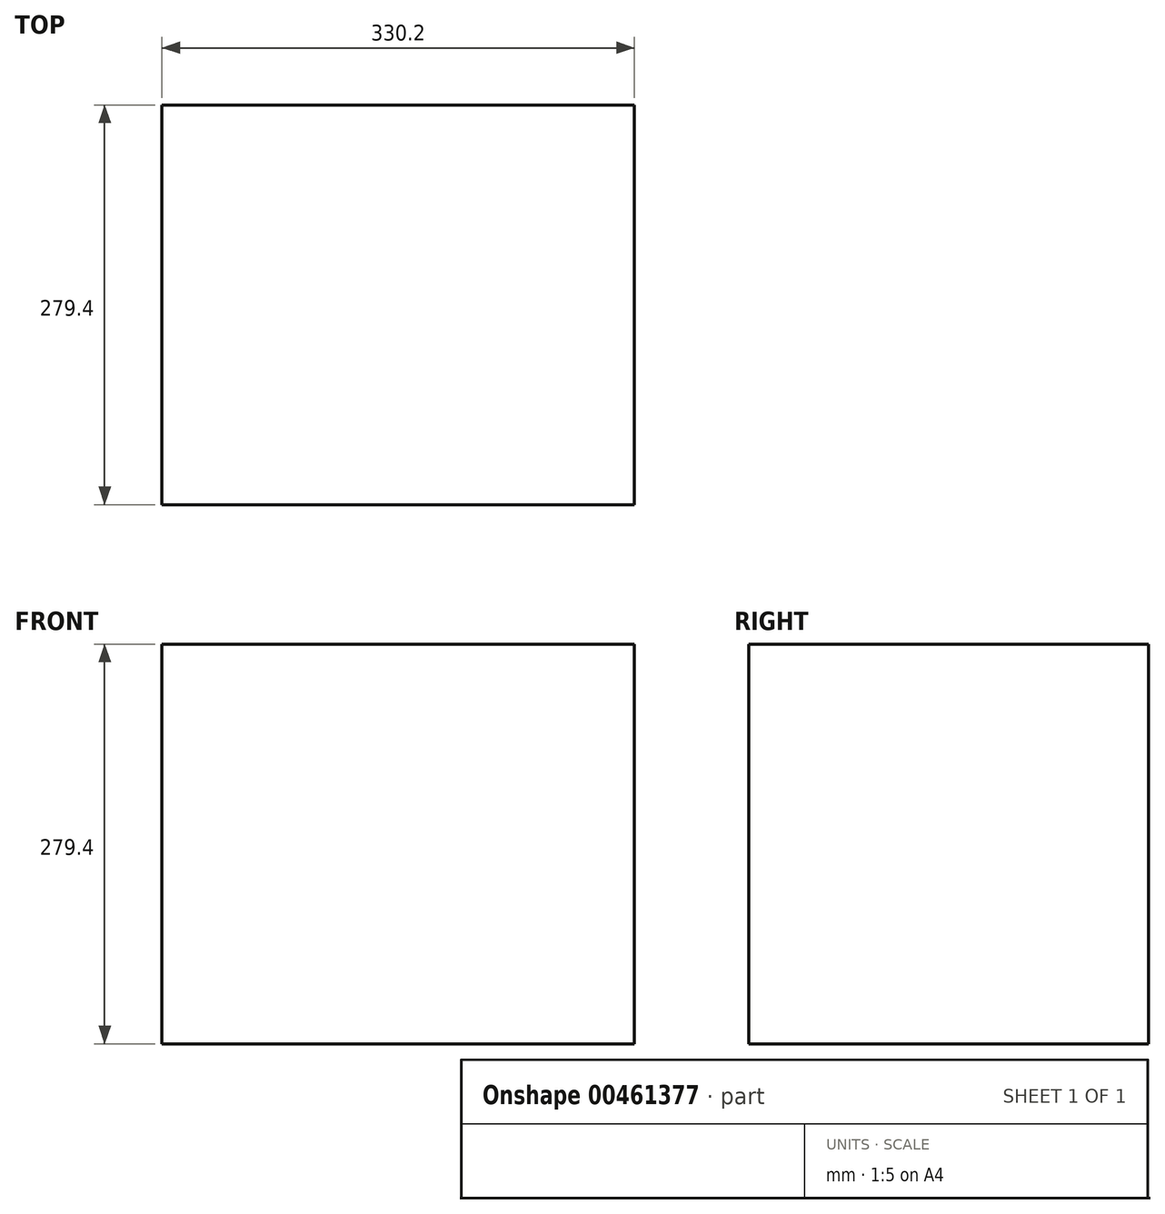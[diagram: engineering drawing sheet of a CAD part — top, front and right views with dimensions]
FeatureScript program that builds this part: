
annotation { "Feature Type Name" : "Feature", "Feature Type Description" : "" }
export const myFeature = defineFeature(function(context is Context, id is Id, definition is map)
    precondition{}
    {
        {
            var Q0;
            Q0=qCreatedBy(makeId("Top.planeOp"),FACE);
            var sketch = newSketch(context, id + "F0", { "sketchPlane" : qUnion([Q0]), "disableImprinting" : false});
            skLineSegment(sketch, "E0.bottom", {"start": v(165.1, 139.7) * mm, "end": v(-165.1, 139.7) * mm});
            skLineSegment(sketch, "E0.top", {"start": v(165.1, -139.7) * mm, "end": v(-165.1, -139.7) * mm});
            skLineSegment(sketch, "E0.left", {"start": v(165.1, 139.7) * mm, "end": v(165.1, -139.7) * mm});
            skLineSegment(sketch, "E0.right", {"start": v(-165.1, 139.7) * mm, "end": v(-165.1, -139.7) * mm});
            skPoint(sketch, "E0.middle", {"position": v(0, 0) * mm});
            skSolve(sketch);
        }
        {
            var Q0;
            Q0 = qSketchRegion(id + "F0", true);
            var Q1;
            Q1=makeQuery(id+"F0.imprint","IMPRINT",FACE,{"disambiguationData":[TD([[makeQuery(id+"F0.imprint","IMPRINT",EDGE,{"derivedFrom":sQuery(id+"F0.wireOp",EDGE,"E0.bottom")}),1.0]])]});
            extrude(context, id + "F1", {"entities" : qUnion([Q0, Q1]), "flatOperationType" : FlatOperationType.REMOVE, "thickness1" : 6.35 * mm, "thickness2" : 0 * mm, "thickness" : 6.35 * mm, "offsetDistance" : 25.4 * mm, "startOffsetBound" : StartOffsetType.BLIND, "startOffsetDistance" : 25.4 * mm, "depth" : 279.4 * mm, "domain" : OperationDomain.MODEL});
        }
    });
